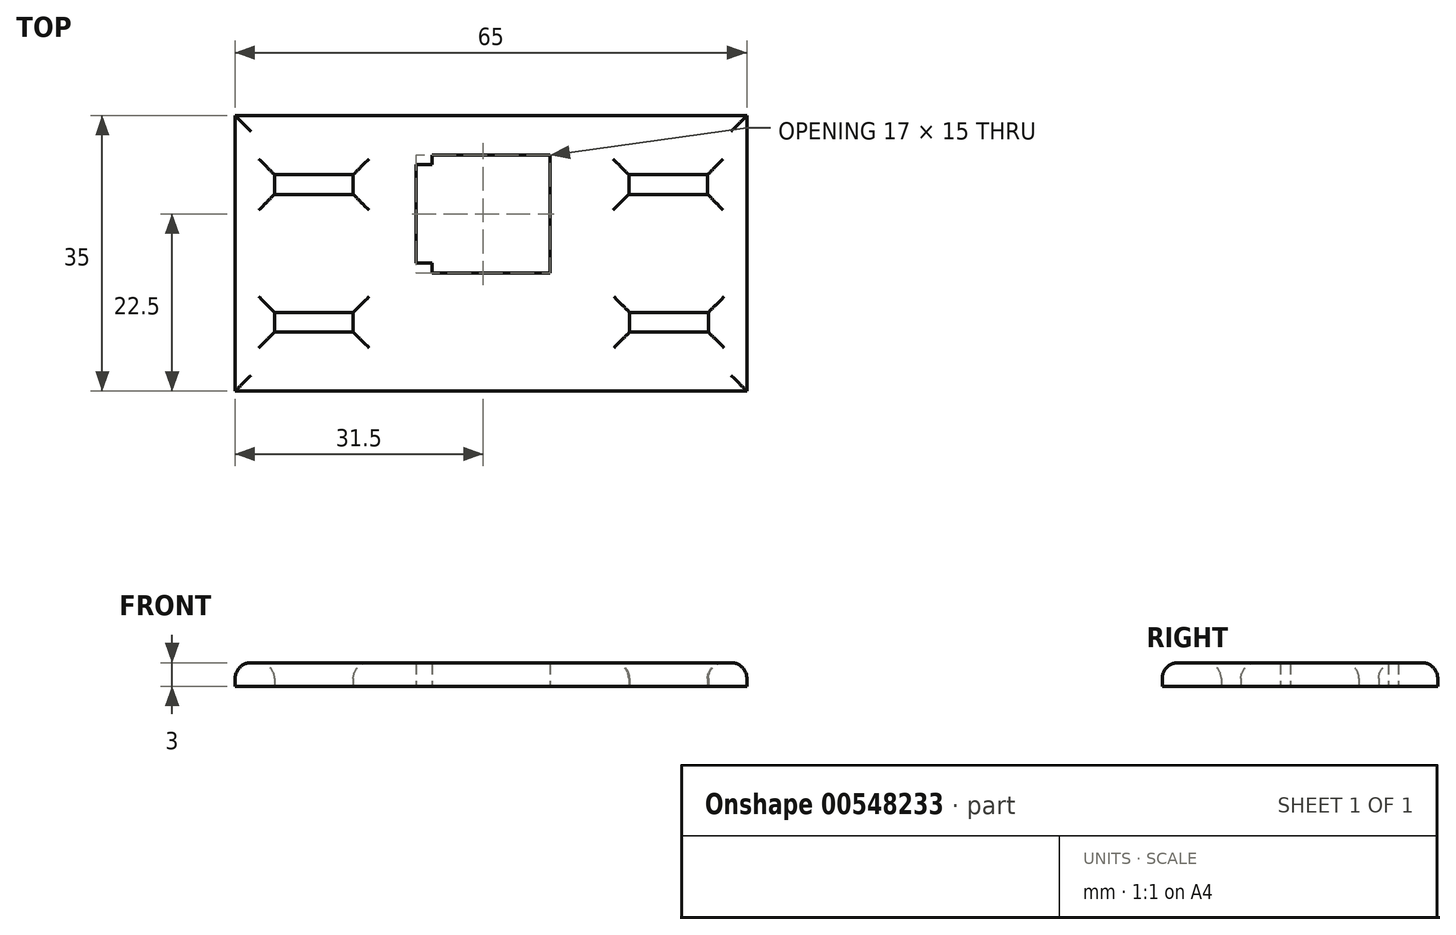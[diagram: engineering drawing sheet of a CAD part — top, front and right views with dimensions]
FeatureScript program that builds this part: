
annotation { "Feature Type Name" : "Feature", "Feature Type Description" : "" }
export const myFeature = defineFeature(function(context is Context, id is Id, definition is map)
    precondition{}
    {
        {
            var Q0;
            Q0=qCreatedBy(makeId("Top.planeOp"),FACE);
            var sketch = newSketch(context, id + "F0", { "sketchPlane" : qUnion([Q0])});
            skLineSegment(sketch, "E0.bottom", {"start": v(32.5, 17.5) * mm, "end": v(-32.5, 17.5) * mm});
            skLineSegment(sketch, "E0.top", {"start": v(32.5, -17.5) * mm, "end": v(-32.5, -17.5) * mm});
            skLineSegment(sketch, "E0.left", {"start": v(32.5, 17.5) * mm, "end": v(32.5, -17.5) * mm});
            skLineSegment(sketch, "E0.right", {"start": v(-32.5, 17.5) * mm, "end": v(-32.5, -17.5) * mm});
            skPoint(sketch, "E0.middle", {"position": v(0, 0) * mm});
            skLineSegment(sketch, "E1.bottom", {"start": v(-7.5, -2.5) * mm, "end": v(7.5, -2.5) * mm});
            skLineSegment(sketch, "E1.top", {"start": v(-7.5, 12.5) * mm, "end": v(7.5, 12.5) * mm});
            skLineSegment(sketch, "E1.right", {"start": v(7.5, -2.5) * mm, "end": v(7.5, 12.5) * mm});
            skLineSegment(sketch, "E2.bottom", {"start": v(-27.5, 7.5) * mm, "end": v(-17.5, 7.5) * mm});
            skLineSegment(sketch, "E2.top", {"start": v(-27.5, 10) * mm, "end": v(-17.5, 10) * mm});
            skLineSegment(sketch, "E2.left", {"start": v(-27.5, 7.5) * mm, "end": v(-27.5, 10) * mm});
            skLineSegment(sketch, "E2.right", {"start": v(-17.5, 7.5) * mm, "end": v(-17.5, 10) * mm});
            skLineSegment(sketch, "E3.bottom", {"start": v(-27.5, -10) * mm, "end": v(-17.5, -10) * mm});
            skLineSegment(sketch, "E3.top", {"start": v(-27.5, -7.5) * mm, "end": v(-17.5, -7.5) * mm});
            skLineSegment(sketch, "E3.left", {"start": v(-27.5, -10) * mm, "end": v(-27.5, -7.5) * mm});
            skLineSegment(sketch, "E3.right", {"start": v(-17.5, -10) * mm, "end": v(-17.5, -7.5) * mm});
            skLineSegment(sketch, "E4.bottom", {"start": v(17.5, 7.5) * mm, "end": v(27.5, 7.5) * mm});
            skLineSegment(sketch, "E4.top", {"start": v(17.5, 10) * mm, "end": v(27.5, 10) * mm});
            skLineSegment(sketch, "E4.left", {"start": v(17.5, 7.5) * mm, "end": v(17.5, 10) * mm});
            skLineSegment(sketch, "E4.right", {"start": v(27.5, 7.5) * mm, "end": v(27.5, 10) * mm});
            skLineSegment(sketch, "E5.bottom", {"start": v(17.6, -7.5) * mm, "end": v(27.6, -7.5) * mm});
            skLineSegment(sketch, "E5.top", {"start": v(17.6, -10) * mm, "end": v(27.6, -10) * mm});
            skLineSegment(sketch, "E5.left", {"start": v(17.6, -7.5) * mm, "end": v(17.6, -10) * mm});
            skLineSegment(sketch, "E5.right", {"start": v(27.6, -7.5) * mm, "end": v(27.6, -10) * mm});
            skLineSegment(sketch, "E6", {"start": v(-27.5, 10) * mm, "end": v(-27.5, 17.5) * mm, "construction": true});
            skLineSegment(sketch, "E7", {"start": v(-27.5, 7.5) * mm, "end": v(-32.5, 7.5) * mm, "construction": true});
            skLineSegment(sketch, "E8", {"start": v(-27.5, -7.5) * mm, "end": v(-32.5, -7.5) * mm, "construction": true});
            skLineSegment(sketch, "E9", {"start": v(-27.5, -7.5) * mm, "end": v(-27.5, 7.5) * mm, "construction": true});
            skLineSegment(sketch, "E10", {"start": v(17.6, -7.5) * mm, "end": v(17.5, 7.5) * mm, "construction": true});
            skLineSegment(sketch, "E11", {"start": v(17.5, 10) * mm, "end": v(17.5, 17.5) * mm, "construction": true});
            skLineSegment(sketch, "E12", {"start": v(27.5, 10) * mm, "end": v(32.5, 10) * mm, "construction": true});
            skLineSegment(sketch, "E13", {"start": v(-27.5, -10) * mm, "end": v(-27.5, -17.5) * mm, "construction": true});
            skLineSegment(sketch, "E14.bottom", {"start": v(-7.5, 11.25) * mm, "end": v(-9.5, 11.25) * mm});
            skLineSegment(sketch, "E14.top", {"start": v(-7.5, -1.25) * mm, "end": v(-9.5, -1.25) * mm});
            skLineSegment(sketch, "E14.right", {"start": v(-9.5, 11.25) * mm, "end": v(-9.5, -1.25) * mm});
            skLineSegment(sketch, "E15", {"start": v(-7.5, -1.25) * mm, "end": v(-7.5, -2.5) * mm});
            skLineSegment(sketch, "E16", {"start": v(-7.5, 11.25) * mm, "end": v(-7.5, 12.5) * mm});
            skLineSegment(sketch, "E17", {"start": v(7.5, -2.5) * mm, "end": v(32.5, -2.5) * mm, "construction": true});
            skSolve(sketch);
        }
        {
            var Q0;
            Q0 = qSketchRegion(id + "F0", true);
            extrude(context, id + "F1", {"entities" : qUnion([Q0]), "depth" : 3 * mm, "offsetDistance" : 25 * mm});
        }
        {
            var Q0;
            Q0=makeQuery(id+"F1.opExtrude","CAP_EDGE",EDGE,{"disambiguationData":[OSD([sQuery(id+"F0.wireOp",EDGE,"E0.bottom")])],"isStart":false});
            var Q1;
            Q1=makeQuery(id+"F1.opExtrude","CAP_EDGE",EDGE,{"disambiguationData":[OSD([sQuery(id+"F0.wireOp",EDGE,"E0.right")])],"isStart":false});
            var Q2;
            Q2=makeQuery(id+"F1.opExtrude","CAP_EDGE",EDGE,{"disambiguationData":[OSD([sQuery(id+"F0.wireOp",EDGE,"E2.top")])],"isStart":false});
            var Q3;
            Q3=makeQuery(id+"F1.opExtrude","CAP_EDGE",EDGE,{"disambiguationData":[OSD([sQuery(id+"F0.wireOp",EDGE,"E2.bottom")])],"isStart":false});
            var Q4;
            Q4=makeQuery(id+"F1.opExtrude","CAP_EDGE",EDGE,{"disambiguationData":[OSD([sQuery(id+"F0.wireOp",EDGE,"E2.left")])],"isStart":false});
            var Q5;
            Q5=makeQuery(id+"F1.opExtrude","CAP_EDGE",EDGE,{"disambiguationData":[OSD([sQuery(id+"F0.wireOp",EDGE,"E2.right")])],"isStart":false});
            var Q6;
            Q6=makeQuery(id+"F1.opExtrude","CAP_EDGE",EDGE,{"disambiguationData":[OSD([sQuery(id+"F0.wireOp",EDGE,"E3.top")])],"isStart":false});
            var Q7;
            Q7=makeQuery(id+"F1.opExtrude","CAP_EDGE",EDGE,{"disambiguationData":[OSD([sQuery(id+"F0.wireOp",EDGE,"E3.left")])],"isStart":false});
            var Q8;
            Q8=makeQuery(id+"F1.opExtrude","CAP_EDGE",EDGE,{"disambiguationData":[OSD([sQuery(id+"F0.wireOp",EDGE,"E3.right")])],"isStart":false});
            var Q9;
            Q9=makeQuery(id+"F1.opExtrude","CAP_EDGE",EDGE,{"disambiguationData":[OSD([sQuery(id+"F0.wireOp",EDGE,"E3.bottom")])],"isStart":false});
            var Q10;
            Q10=makeQuery(id+"F1.opExtrude","CAP_EDGE",EDGE,{"disambiguationData":[OSD([sQuery(id+"F0.wireOp",EDGE,"E5.top")])],"isStart":false});
            var Q11;
            Q11=makeQuery(id+"F1.opExtrude","CAP_EDGE",EDGE,{"disambiguationData":[OSD([sQuery(id+"F0.wireOp",EDGE,"E5.left")])],"isStart":false});
            var Q12;
            Q12=makeQuery(id+"F1.opExtrude","CAP_EDGE",EDGE,{"disambiguationData":[OSD([sQuery(id+"F0.wireOp",EDGE,"E5.bottom")])],"isStart":false});
            var Q13;
            Q13=makeQuery(id+"F1.opExtrude","CAP_EDGE",EDGE,{"disambiguationData":[OSD([sQuery(id+"F0.wireOp",EDGE,"E5.right")])],"isStart":false});
            var Q14;
            Q14=makeQuery(id+"F1.opExtrude","CAP_EDGE",EDGE,{"disambiguationData":[OSD([sQuery(id+"F0.wireOp",EDGE,"E4.bottom")])],"isStart":false});
            var Q15;
            Q15=makeQuery(id+"F1.opExtrude","CAP_EDGE",EDGE,{"disambiguationData":[OSD([sQuery(id+"F0.wireOp",EDGE,"E4.left")])],"isStart":false});
            var Q16;
            Q16=makeQuery(id+"F1.opExtrude","CAP_EDGE",EDGE,{"disambiguationData":[OSD([sQuery(id+"F0.wireOp",EDGE,"E4.top")])],"isStart":false});
            var Q17;
            Q17=makeQuery(id+"F1.opExtrude","CAP_EDGE",EDGE,{"disambiguationData":[OSD([sQuery(id+"F0.wireOp",EDGE,"E4.right")])],"isStart":false});
            var Q18;
            Q18=makeQuery(id+"F1.opExtrude","CAP_EDGE",EDGE,{"disambiguationData":[OSD([sQuery(id+"F0.wireOp",EDGE,"E0.left")])],"isStart":false});
            var Q19;
            Q19=makeQuery(id+"F1.opExtrude","CAP_EDGE",EDGE,{"disambiguationData":[OSD([sQuery(id+"F0.wireOp",EDGE,"E0.top")])],"isStart":false});
            fillet(context, id + "F2", {"entities" : qUnion([Q0, Q1, Q2, Q3, Q4, Q5, Q6, Q7, Q8, Q9, Q10, Q11, Q12, Q13, Q14, Q15, Q16, Q17, Q18, Q19]), "radius" : 2 * mm, "tangentPropagation" : true, "allowEdgeOverflow" : false});
        }
    });
